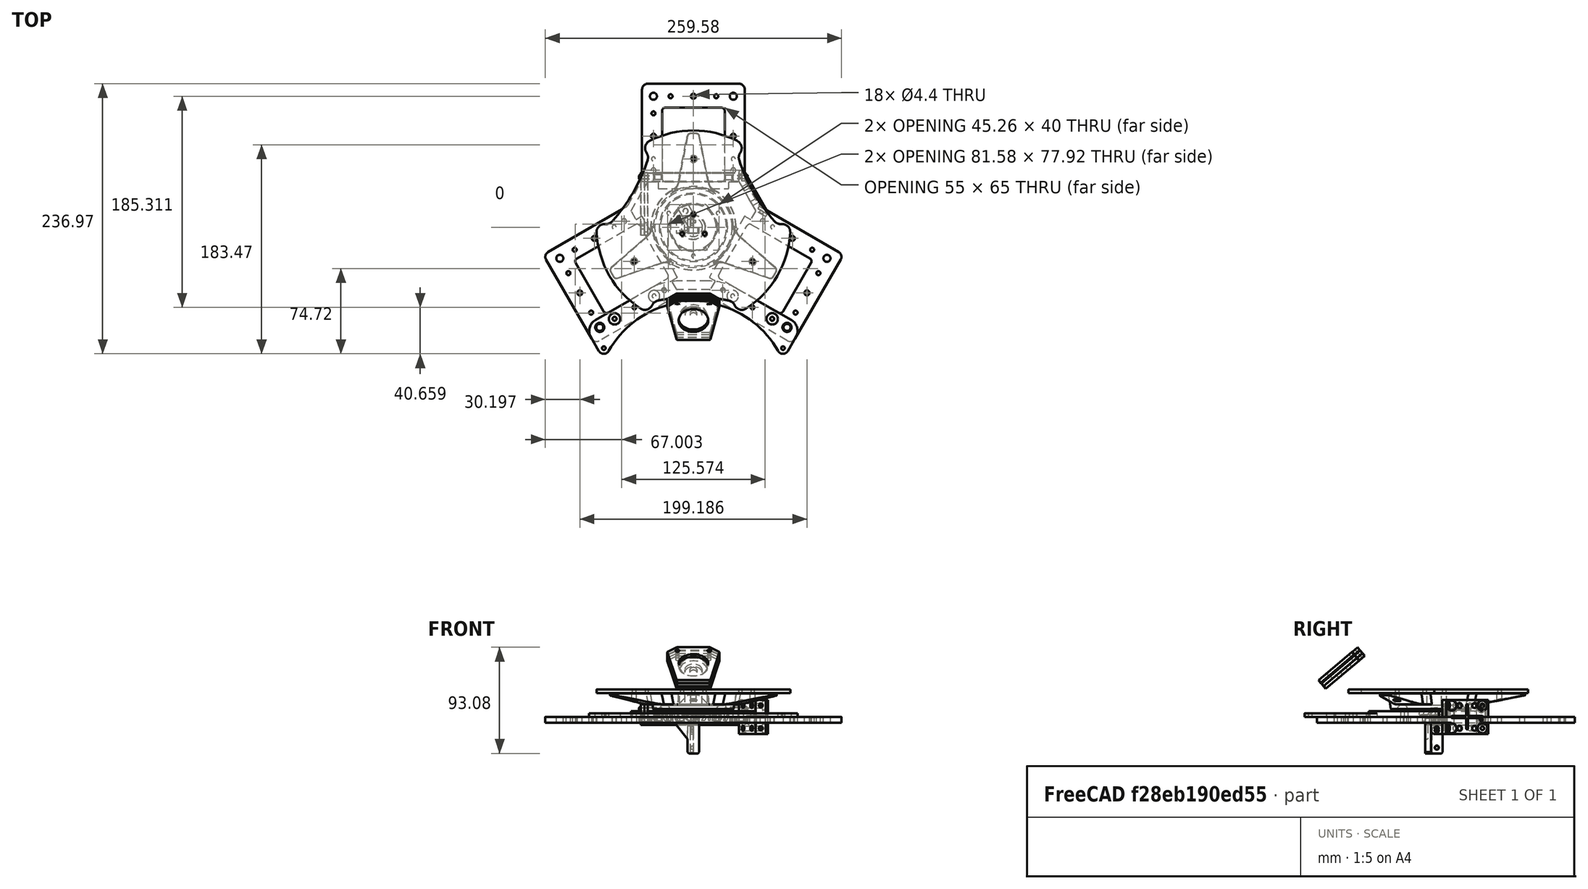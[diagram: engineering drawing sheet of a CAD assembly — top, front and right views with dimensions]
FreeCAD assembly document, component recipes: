
FREECAD ASSEMBLY — COMPONENT RECIPES ("structures")

This assembly document has 14 components, labeled P0..P13 below (a component is one placed body or linked part). 12 of them carry a construction recipe — the FreeCAD feature program that regenerates the part from scratch, quoted from this document or its linked companion documents; the rest are supplied as boundary geometry only. No exploded tour is included for this assembly.
NOTE — document 2 of 2 of this assembly tour. The two overview renders and the header above are repeated from document 1; the component sections below continue where the previous document stopped.
COMPONENT P11 — recipe-attached ("CoinTirette", modeled in this document).
Construction recipe (the document's own serialized feature program — sketch geometry with constraints, then the solid features built on it; lengths are millimeters unless a unit is written):

FEATURE [PartDesign::FeatureBase] Clone
  BaseFeature = -> Body030
  InvalidShape = false
  NewSolid = false
  Suppress = false
  TreeRank = 0
  ValidateShape = true
FEATURE [Sketcher::SketchObject] Sketch068
  ArcFitTolerance = 0
  AttachmentSupport = -> [Clone]
  ExternalBSplineMaxDegree = 0
  ExternalBSplineTolerance = 0
  ExternalGeometry = -> [Clone]
  FullyConstrained = true
  InternalTolerance = 1e-06
  InvalidShape = false
  MakeInternals = false
  MapMode = 5
  Placement = pos=(-3.09e-14,-52.3388,62.375) rot=(1,0,0;0.698132rad)
  Support = -> [Clone]
  TreeRank = 0
  ValidateShape = true
  sketch-geometry (2):
    g0: Circle CenterX=0 CenterY=-32.5627 CenterZ=0 NormalX=0 NormalY=0 NormalZ=1 AngleXU=0 Radius=3
    g1: Circle CenterX=0 CenterY=-32.5627 CenterZ=0 NormalX=0 NormalY=0 NormalZ=1 AngleXU=0 Radius=15
  constraints (4):
    c: Coincident(g0,g-3)
    c: Coincident(g1,g0)
    c: Diameter(g1) = 30
    c: Diameter(g0) = 6
FEATURE [PartDesign::Pad] Pad037
  AddSubType = 0
  AutoTaperInnerAngle = false
  BaseFeature = -> Clone
  CheckUpToFaceLimits = true
  ClaimChildren = false
  Direction = (-4e-16,-0.642788,0.766044)
  Fit = 0
  FitJoin = 0
  InnerFit = 0
  InnerFitJoin = 0
  InvalidShape = false
  Length = 10
  Length2 = 100
  Linearize = true
  NewSolid = false
  Profile = -> Sketch068
  Refine = true
  Suppress = false
  TaperInnerAngle = 0
  TaperInnerAngleRev = 0
  TreeRank = 0
  Type = 3
  UpToFace = -> Clone [Face2]
  ValidateShape = true
  _ProfileBasedVersion = 1
FEATURE [PartDesign::Body] Body032  label="PlateTirette_1"
  AutoGroupSolids = false
  BaseFeature = -> Body030
  ClaimAllChildren = false
  ExportMode = 0
  Group = -> [Clone,Sketch068,Pad037]
  InvalidShape = false
  Origin = -> Origin051
  SingleSolid = true
  Tip = -> Pad037
  TreeRank = 0
  ValidateShape = true
  _ExportChildren = -> [Clone,Pad037]
  _GroupVersion = 1
FEATURE [PartDesign::SubShapeBinder] Binder001  label="Binder001(Pad037)"
  BindCopyOnChange = 0
  BindMode = 2
  ClaimChildren = false
  Context = -> Part011 [Body033.Binder001.]
  EdgeTolerance = 1e-06
  FillStyle = 0
  Fuse = false
  InvalidShape = false
  MakeFace = true
  MergeEdges = true
  OffsetFill = false
  OffsetIntersection = false
  OffsetJoinType = 0
  OffsetOpenResult = false
  Outline = false
  PartialLoad = false
  Refine = true
  Relative = true
  SplitEdges = false
  TightBound = false
  TreeRank = 0
  ValidateShape = true
  _Version = 8
FEATURE [PartDesign::Pad] Pad038
  AddSubType = 0
  AutoTaperInnerAngle = false
  CheckUpToFaceLimits = true
  ClaimChildren = false
  Direction = (-4e-16,-0.642788,0.766044)
  Fit = 0
  FitJoin = 0
  InnerFit = 0
  InnerFitJoin = 0
  InvalidShape = false
  Length = 3
  Length2 = 100
  Linearize = true
  NewSolid = false
  Profile = -> Binder001
  Refine = true
  Suppress = false
  TaperInnerAngle = 0
  TaperInnerAngleRev = 0
  TreeRank = 0
  Type = 0
  ValidateShape = true
  _ProfileBasedVersion = 1
FEATURE [Sketcher::SketchObject] Sketch069
  ArcFitTolerance = 0
  AttachmentSupport = -> [Pad038]
  ExternalBSplineMaxDegree = 0
  ExternalBSplineTolerance = 0
  ExternalGeometry = -> [Pad038]
  FullyConstrained = true
  InternalTolerance = 1e-06
  InvalidShape = false
  MakeInternals = false
  MapMode = 5
  Placement = pos=(-3.46e-14,-54.2672,64.6731) rot=(1,0,0;0.698132rad)
  Support = -> [Pad038]
  TreeRank = 0
  ValidateShape = true
  sketch-geometry (1):
    g0: Circle CenterX=0 CenterY=-32.5627 CenterZ=0 NormalX=0 NormalY=0 NormalZ=1 AngleXU=0 Radius=12
  constraints (2):
    c: Coincident(g0,g-3)
    c: Diameter(g0) = 24
FEATURE [PartDesign::Pocket] Pocket030
  AddSubType = 1
  AutoTaperInnerAngle = false
  BaseFeature = -> Pad038
  CheckUpToFaceLimits = true
  ClaimChildren = false
  Direction = (1,1,1)
  Fit = 0
  FitJoin = 0
  InnerFit = 0
  InnerFitJoin = 0
  InvalidShape = false
  Length = 5
  Length2 = 100
  Linearize = true
  NewSolid = false
  Profile = -> Sketch069
  Refine = true
  Suppress = false
  TaperInnerAngle = 0
  TaperInnerAngleRev = 0
  TreeRank = 0
  Type = 1
  ValidateShape = true
  _ProfileBasedVersion = 1
  _Version = 1
FEATURE [PartDesign::Body] Body033  label="PlateTirette_2"
  AutoGroupSolids = false
  ClaimAllChildren = false
  ExportMode = 0
  Group = -> [Binder001,Pad038,Sketch069,Pocket030]
  InvalidShape = false
  Origin = -> Origin052
  SingleSolid = true
  Tip = -> Pocket030
  TreeRank = 0
  ValidateShape = true
  _ExportChildren = -> [Pad038,Pocket030]
  _GroupVersion = 1
FEATURE [PartDesign::SubShapeBinder] Binder002  label="Binder002(Pocket030)"
  BindCopyOnChange = 0
  BindMode = 0
  ClaimChildren = false
  Context = -> Part011 [Body034.Binder002.]
  EdgeTolerance = 1e-06
  FillStyle = 0
  Fuse = false
  InvalidShape = false
  MakeFace = true
  MergeEdges = true
  OffsetFill = false
  OffsetIntersection = false
  OffsetJoinType = 0
  OffsetOpenResult = false
  Outline = false
  PartialLoad = false
  Refine = true
  Relative = true
  SplitEdges = false
  Support = -> [Body033[Pocket030.Face5]]
  TightBound = false
  TreeRank = 0
  ValidateShape = true
  _Version = 8
FEATURE [PartDesign::Pad] Pad039
  AddSubType = 0
  AutoTaperInnerAngle = false
  CheckUpToFaceLimits = true
  ClaimChildren = false
  Direction = (-4e-16,-0.642788,0.766044)
  Fit = 0
  FitJoin = 0
  InnerFit = 0
  InnerFitJoin = 0
  InvalidShape = false
  Length = 0.8
  Length2 = 100
  Linearize = true
  NewSolid = false
  Profile = -> Binder002
  Refine = true
  Suppress = false
  TaperInnerAngle = 0
  TaperInnerAngleRev = 0
  TreeRank = 0
  Type = 0
  ValidateShape = true
  _ProfileBasedVersion = 1
FEATURE [Sketcher::SketchObject] Sketch070
  ArcFitTolerance = 0
  AttachmentSupport = -> [Pad039]
  ExternalBSplineMaxDegree = 0
  ExternalBSplineTolerance = 0
  ExternalGeometry = -> [Pad039]
  FullyConstrained = true
  InternalTolerance = 1e-06
  InvalidShape = false
  MakeInternals = false
  MapMode = 5
  Placement = pos=(-3.49e-14,-54.7814,65.286) rot=(1,0,0;0.698132rad)
  Support = -> [Pad039]
  TreeRank = 0
  ValidateShape = true
  sketch-geometry (1):
    g0: Circle CenterX=0 CenterY=-32.5627 CenterZ=0 NormalX=0 NormalY=0 NormalZ=1 AngleXU=0 Radius=15
  constraints (2):
    c: Coincident(g0,g-3)
    c: Diameter(g0) = 30
FEATURE [PartDesign::Pad] Pad040
  AddSubType = 0
  AutoTaperInnerAngle = false
  BaseFeature = -> Pad039
  CheckUpToFaceLimits = true
  ClaimChildren = false
  Direction = (-4e-16,-0.642788,0.766044)
  Fit = 0
  FitJoin = 0
  InnerFit = 0
  InnerFitJoin = 0
  InvalidShape = false
  Length = 10
  Length2 = 100
  Linearize = true
  NewSolid = false
  Profile = -> Sketch070
  Refine = true
  Reversed = true
  Suppress = false
  TaperInnerAngle = 0
  TaperInnerAngleRev = 0
  TreeRank = 0
  Type = 3
  UpToFace = -> Pad039 [Face16]
  ValidateShape = true
  _ProfileBasedVersion = 1
FEATURE [PartDesign::Body] Body034  label="InterPlateTirette"
  AutoGroupSolids = false
  ClaimAllChildren = false
  ExportMode = 0
  Group = -> [Binder002,Pad039,Sketch070,Pad040]
  InvalidShape = false
  Origin = -> Origin053
  SingleSolid = true
  Tip = -> Pad040
  TreeRank = 0
  ValidateShape = true
  _ExportChildren = -> [Pad039,Pad040]
  _GroupVersion = 1
FEATURE [PartDesign::SubShapeBinder] Binder003  label="Binder003(Pad040)"
  BindCopyOnChange = 0
  BindMode = 2
  ClaimChildren = false
  Context = -> Part011 [Body035.Binder003.]
  EdgeTolerance = 1e-06
  FillStyle = 0
  Fuse = false
  InvalidShape = false
  MakeFace = true
  MergeEdges = true
  OffsetFill = false
  OffsetIntersection = false
  OffsetJoinType = 0
  OffsetOpenResult = false
  Outline = false
  PartialLoad = false
  Refine = true
  Relative = true
  SplitEdges = false
  TightBound = false
  TreeRank = 0
  ValidateShape = true
  _Version = 8
FEATURE [PartDesign::Pad] Pad041
  AddSubType = 0
  AutoTaperInnerAngle = false
  CheckUpToFaceLimits = true
  ClaimChildren = false
  Direction = (-4e-16,-0.642788,0.766044)
  Fit = 0
  FitJoin = 0
  InnerFit = 0
  InnerFitJoin = 0
  InvalidShape = false
  Length = 3
  Length2 = 100
  Linearize = true
  NewSolid = false
  Profile = -> Binder003
  Refine = true
  Suppress = false
  TaperInnerAngle = 0
  TaperInnerAngleRev = 0
  TreeRank = 0
  Type = 0
  ValidateShape = true
  _ProfileBasedVersion = 1
FEATURE [Part::SubShapeBinder] Import  label="Import(Pocket030)"
  BindCopyOnChange = 0
  BindMode = 0
  ClaimChildren = false
  Context = -> Part011 [Body035.Import.]
  EdgeTolerance = 1e-06
  FillStyle = 0
  Fuse = false
  InvalidShape = false
  MakeFace = false
  MergeEdges = true
  OffsetFill = false
  OffsetIntersection = false
  OffsetJoinType = 0
  OffsetOpenResult = false
  Outline = false
  PartialLoad = false
  Refine = true
  Relative = true
  SplitEdges = false
  Support = -> [Body033[Pocket030.]]
  TightBound = false
  TreeRank = 0
  ValidateShape = true
  _Version = 8
FEATURE [Sketcher::SketchObject] Sketch071
  ArcFitTolerance = 0
  AttachmentSupport = -> [Pad041]
  ExternalBSplineMaxDegree = 0
  ExternalBSplineTolerance = 0
  ExternalGeometry = -> [Import]
  FullyConstrained = true
  InternalTolerance = 1e-06
  InvalidShape = false
  MakeInternals = false
  MapMode = 5
  Placement = pos=(-3.62e-14,-56.7098,67.5841) rot=(1,0,0;0.698132rad)
  Support = -> [Pad041]
  TreeRank = 0
  ValidateShape = true
  sketch-geometry (2):
    g0: Circle CenterX=0 CenterY=-32.5627 CenterZ=0 NormalX=0 NormalY=0 NormalZ=1 AngleXU=0 Radius=13
    g1: LineSegment [constr] StartX=-1.96e-14 StartY=-55.0073 StartZ=0 EndX=1.98e-14 EndY=-10.1181 EndZ=0
  constraints (5):
    c: PointOnObject(g0,g-2)
    c: Diameter(g0) = 26
    c: PointOnObject(g1,g-4)
    c: Symmetric(g-3,g-3,g1)
    c: Symmetric(g1,g1,g0)
FEATURE [PartDesign::Pocket] Pocket031
  AddSubType = 1
  AutoTaperInnerAngle = false
  BaseFeature = -> Pad041
  CheckUpToFaceLimits = true
  ClaimChildren = false
  Direction = (1,1,1)
  Fit = 0
  FitJoin = 0
  InnerFit = 0
  InnerFitJoin = 0
  InvalidShape = false
  Length = 5
  Length2 = 100
  Linearize = true
  NewSolid = false
  Profile = -> Sketch071
  Refine = true
  Suppress = false
  TaperInnerAngle = 0
  TaperInnerAngleRev = 0
  TreeRank = 0
  Type = 1
  ValidateShape = true
  _ProfileBasedVersion = 1
  _Version = 1
FEATURE [PartDesign::Body] Body035  label="PlateTirette_3"
  AutoGroupSolids = false
  ClaimAllChildren = false
  ExportMode = 0
  Group = -> [Binder003,Pad041,Sketch071,Import,Pocket031]
  InvalidShape = false
  Origin = -> Origin054
  SingleSolid = true
  Tip = -> Pocket031
  TreeRank = 0
  ValidateShape = true
  _ExportChildren = -> [Pad041,Import,Pocket031]
  _GroupVersion = 1
COMPONENT P12 — recipe-attached ("CoinLogo", modeled in this document).
Construction recipe (the document's own serialized feature program — sketch geometry with constraints, then the solid features built on it; lengths are millimeters unless a unit is written):

FEATURE [PartDesign::SubShapeBinder] Binder004  label="Binder004(Chamfer023)"
  BindCopyOnChange = 0
  BindMode = 0
  ClaimChildren = false
  Context = -> Part012 [Body036.Binder004.]
  EdgeTolerance = 1e-06
  FillStyle = 0
  Fuse = false
  InvalidShape = false
  MakeFace = true
  MergeEdges = true
  OffsetFill = false
  OffsetIntersection = false
  OffsetJoinType = 0
  OffsetOpenResult = false
  Outline = false
  PartialLoad = false
  Refine = true
  Relative = true
  SplitEdges = false
  Support = -> [Chamfer023[Face30]]
  TightBound = false
  TreeRank = 0
  ValidateShape = true
  _Version = 8
FEATURE [Sketcher::SketchObject] Sketch072
  ArcFitTolerance = 0
  AttachmentSupport = -> [Binder004]
  ExternalBSplineMaxDegree = 0
  ExternalBSplineTolerance = 0
  ExternalGeometry = -> [Binder004]
  FullyConstrained = true
  InternalTolerance = 1e-06
  InvalidShape = false
  MakeInternals = false
  MapMode = 5
  Placement = pos=(-2.82e-14,-50.4105,60.0769) rot=(1,0,0;0.698132rad)
  Support = -> [Binder004]
  TreeRank = 0
  ValidateShape = true
  sketch-geometry (2):
    g0: Circle CenterX=-14 CenterY=-14.7181 CenterZ=0 NormalX=0 NormalY=0 NormalZ=1 AngleXU=0 Radius=1.6
    g1: Circle CenterX=14 CenterY=-14.7181 CenterZ=0 NormalX=0 NormalY=0 NormalZ=1 AngleXU=0 Radius=1.6
  constraints (4):
    c: Coincident(g0,g-10)
    c: Coincident(g1,g-9)
    c: Diameter(g1) = 3.2
    c: Equal(g1,g0)
FEATURE [PartDesign::Pad] Pad042
  AddSubType = 0
  AutoTaperInnerAngle = false
  CheckUpToFaceLimits = true
  ClaimChildren = false
  Direction = (1,1,1)
  Fit = 0
  FitJoin = 0
  InnerFit = 0
  InnerFitJoin = 0
  InvalidShape = false
  Length = 3
  Length2 = 100
  Linearize = true
  NewSolid = false
  Profile = -> Sketch072
  Refine = true
  Suppress = false
  TaperInnerAngle = 0
  TaperInnerAngleRev = 0
  TreeRank = 0
  Type = 0
  ValidateShape = true
  _ProfileBasedVersion = 1
FEATURE [Part::Part2DObjectPython] ShapeString001  # Draft 2D object (typed FeaturePython)
  FontFile = <userpath>/Downloads/baveuse/baveuse.ttf
  InvalidShape = false
  Placement = pos=(-9,-91.52,42.09) rot=(1,0,0;0.698132rad)
  Size = 10
  String = K
  Tracking = 0
  TreeRank = 0
  ValidateShape = true
FEATURE [PartDesign::SubShapeBinder] Import001  label="Import001(ShapeString001)"
  BindCopyOnChange = 0
  BindMode = 0
  ClaimChildren = false
  Context = -> Part012 [Body036.Import001.]
  EdgeTolerance = 1e-06
  FillStyle = 0
  Fuse = false
  InvalidShape = false
  MakeFace = false
  MergeEdges = true
  OffsetFill = false
  OffsetIntersection = false
  OffsetJoinType = 0
  OffsetOpenResult = false
  Outline = false
  PartialLoad = false
  Refine = true
  Relative = true
  SplitEdges = false
  Support = -> [ShapeString001]
  TightBound = false
  TreeRank = 0
  ValidateShape = true
  _Version = 8
FEATURE [PartDesign::Pocket] Pocket032
  AddSubType = 1
  AutoTaperInnerAngle = false
  BaseFeature = -> Pad042
  CheckUpToFaceLimits = true
  ClaimChildren = false
  Direction = (1,1,1)
  Fit = 0
  FitJoin = 0
  InnerFit = 0
  InnerFitJoin = 0
  InvalidShape = false
  Length = 10
  Length2 = 100
  Linearize = true
  NewSolid = false
  Profile = -> Import001
  Refine = true
  Suppress = false
  TaperInnerAngle = 0
  TaperInnerAngleRev = 0
  TreeRank = 0
  Type = 0
  ValidateShape = true
  _ProfileBasedVersion = 1
  _Version = 1
FEATURE [PartDesign::Chamfer] Chamfer024
  AddSubType = 0
  Angle = 45
  Base = -> Pocket032 [Edge48,Edge49,Edge8,Edge5,Edge1,Edge2]
  BaseFeature = -> Pocket032
  ChamferType = 0
  FlipDirection = false
  InvalidShape = false
  NewSolid = false
  Refine = true
  Size = 0.4
  Size2 = 1
  SupportTransform = false
  Suppress = false
  TreeRank = 0
  UseAllEdges = false
  ValidateShape = true
FEATURE [PartDesign::Body] Body036  label="PlateLogo"
  AutoGroupSolids = false
  ClaimAllChildren = false
  ExportMode = 0
  Group = -> [Binder004,Sketch072,Pad042,ShapeString001,Import001,Pocket032,Chamfer024]
  InvalidShape = false
  Origin = -> Origin056
  SingleSolid = true
  Tip = -> Chamfer024
  TreeRank = 0
  ValidateShape = true
  _ExportChildren = -> [Binder004,Pad042,ShapeString001,Pocket032,Chamfer024]
  _GroupVersion = 1
FEATURE [PartDesign::FeatureBase] Clone001
  BaseFeature = -> Pad042
  InvalidShape = false
  NewSolid = false
  Suppress = false
  TreeRank = 10
  ValidateShape = true
FEATURE [Sketcher::SketchObject] Sketch073
  ArcFitTolerance = 0
  AttachmentSupport = -> [Clone001]
  ExternalBSplineMaxDegree = 0
  ExternalBSplineTolerance = 0
  ExternalGeometry = -> [Clone001]
  FullyConstrained = true
  InternalTolerance = 1e-06
  InvalidShape = false
  MakeInternals = false
  MapMode = 5
  Placement = pos=(-3.18e-14,-52.3388,62.375) rot=(1,0,0;0.698132rad)
  Support = -> [Clone001]
  TreeRank = 12
  ValidateShape = true
  sketch-geometry (1):
    g0: Circle CenterX=0 CenterY=-32.5673 CenterZ=0 NormalX=0 NormalY=0 NormalZ=1 AngleXU=0 Radius=7.5
  constraints (3):
    c: PointOnObject(g0,g-2)
    c: DistanceY(g-3,g0) = 22.44
    c: Diameter(g0) = 15
FEATURE [PartDesign::Pocket] Pocket033
  AddSubType = 1
  AutoTaperInnerAngle = false
  BaseFeature = -> Clone001
  CheckUpToFaceLimits = true
  ClaimChildren = false
  Direction = (1,1,1)
  Fit = 0
  FitJoin = 0
  InnerFit = 0
  InnerFitJoin = 0
  InvalidShape = false
  Length = 5
  Length2 = 100
  Linearize = true
  NewSolid = false
  Profile = -> Sketch073
  Refine = true
  Suppress = false
  TaperInnerAngle = 0
  TaperInnerAngleRev = 0
  TreeRank = 13
  Type = 1
  ValidateShape = true
  _ProfileBasedVersion = 1
  _Version = 1
FEATURE [PartDesign::Body] Body037  label="PlateInit"
  AutoGroupSolids = false
  BaseFeature = -> Pad042
  ClaimAllChildren = false
  ExportMode = 0
  Group = -> [Clone001,Sketch073,Pocket033]
  InvalidShape = false
  Origin = -> Origin057
  SingleSolid = true
  Tip = -> Pocket033
  TreeRank = 11
  ValidateShape = true
  _ExportChildren = -> [Clone001,Pocket033]
  _GroupVersion = 1
COMPONENT P13 — recipe-attached ("RobotStand", modeled in this document).
Construction recipe (the document's own serialized feature program — sketch geometry with constraints, then the solid features built on it; lengths are millimeters unless a unit is written):

FEATURE [Sketcher::SketchObject] Sketch074
  ArcFitTolerance = 1e-06
  AttachmentSupport = -> [XY_Plane047]
  ExternalBSplineMaxDegree = 5
  ExternalBSplineTolerance = 0.0001
  FullyConstrained = true
  InternalTolerance = 1e-06
  InvalidShape = false
  MakeInternals = true
  MapMode = 5
  Support = -> [XY_Plane047]
  TreeRank = 105
  ValidateShape = true
  sketch-geometry (1):
    g0: Circle CenterX=0 CenterY=0 CenterZ=0 NormalX=0 NormalY=0 NormalZ=1 AngleXU=0 Radius=10
  constraints (2):
    c: Coincident(g0,g-1)
    c: Diameter(g0) = 20
FEATURE [PartDesign::Pad] Pad043
  AddSubType = 0
  AlongSketchNormal = false
  AutoTaperInnerAngle = true
  CheckUpToFaceLimits = true
  ClaimChildren = false
  Direction = (0,0,1)
  Fit = 0
  FitJoin = 0
  InnerFit = 0
  InnerFitJoin = 0
  InvalidShape = false
  Length = 4
  Length2 = 100
  Linearize = true
  NewSolid = false
  Profile = -> Sketch074
  Refine = true
  Suppress = false
  TaperAngle = 10
  TaperInnerAngle = -10
  TaperInnerAngleRev = 0
  TreeRank = 106
  Type = 0
  ValidateShape = true
  _ProfileBasedVersion = 1
FEATURE [PartDesign::Pad] Pad044
  AddSubType = 0
  AlongSketchNormal = false
  AutoTaperInnerAngle = true
  BaseFeature = -> Pad043
  CheckUpToFaceLimits = true
  ClaimChildren = false
  Direction = (0,0,1)
  Fit = 0
  FitJoin = 0
  InnerFit = 0
  InnerFitJoin = 0
  InvalidShape = false
  Length = 2
  Length2 = 100
  Linearize = true
  NewSolid = false
  Profile = -> Pad043 [Face3]
  Refine = true
  Suppress = false
  TaperInnerAngle = 0
  TaperInnerAngleRev = 0
  TreeRank = 107
  Type = 0
  ValidateShape = true
  _ProfileBasedVersion = 1
FEATURE [Sketcher::SketchObject] Sketch075
  ArcFitTolerance = 1e-06
  AttachmentSupport = -> [Pad044]
  ExternalBSplineMaxDegree = 5
  ExternalBSplineTolerance = 0.0001
  FullyConstrained = true
  InternalTolerance = 1e-06
  InvalidShape = false
  MakeInternals = true
  MapMode = 5
  Placement = pos=(0,0,6) rot=(0,0,1;0rad)
  Support = -> [Pad044]
  TreeRank = 108
  ValidateShape = true
  sketch-geometry (1):
    g0: Circle CenterX=0 CenterY=0 CenterZ=0 NormalX=0 NormalY=0 NormalZ=1 AngleXU=0 Radius=35
  constraints (2):
    c: Coincident(g0,g-1)
    c: Diameter(g0) = 70
FEATURE [PartDesign::Pad] Pad045
  AddSubType = 0
  AlongSketchNormal = false
  AutoTaperInnerAngle = true
  BaseFeature = -> Pad044
  CheckUpToFaceLimits = true
  ClaimChildren = false
  Direction = (0,0,1)
  Fit = 0
  FitJoin = 0
  InnerFit = 0
  InnerFitJoin = 0
  InvalidShape = false
  Length = 15
  Length2 = 100
  Linearize = true
  NewSolid = false
  Profile = -> Sketch075
  Refine = true
  Suppress = false
  TaperAngle = 10
  TaperInnerAngle = -10
  TaperInnerAngleRev = 0
  TreeRank = 109
  Type = 0
  ValidateShape = true
  _ProfileBasedVersion = 1
FEATURE [Part::SubShapeBinder] Import002  label="Import002(Fillet011)"
  BindCopyOnChange = 0
  BindMode = 0
  ClaimChildren = false
  Context = -> Group002 [Body038.Import002.]
  EdgeTolerance = 1e-06
  FillStyle = 0
  Fuse = false
  InvalidShape = false
  MakeFace = false
  MergeEdges = true
  OffsetFill = false
  OffsetIntersection = false
  OffsetJoinType = 0
  OffsetOpenResult = false
  Outline = false
  PartialLoad = false
  Relative = true
  SplitEdges = false
  Support = -> [Link075[Fillet011.]]
  TightBound = false
  TreeRank = 110
  ValidateShape = true
  _Version = 8
FEATURE [Sketcher::SketchObject] Sketch076
  ArcFitTolerance = 1e-06
  AttachmentSupport = -> [YZ_Plane047]
  ExternalBSplineMaxDegree = 5
  ExternalBSplineTolerance = 0.0001
  ExternalGeometry = -> [Pad045]
  FullyConstrained = true
  InternalTolerance = 1e-06
  InvalidShape = false
  MakeInternals = true
  MapMode = 5
  Placement = pos=(0,0,0) rot=(0.57735,0.57735,0.57735;2.0944rad)
  Support = -> [YZ_Plane047]
  TreeRank = 111
  ValidateShape = true
  sketch-geometry (5):
    g0: LineSegment StartX=21 StartY=6 StartZ=0 EndX=29 EndY=6 EndZ=0
    g1: LineSegment StartX=29 StartY=6 StartZ=0 EndX=29 EndY=10 EndZ=0
    g2: LineSegment StartX=29 StartY=10 StartZ=0 EndX=21 EndY=10 EndZ=0
    g3: LineSegment StartX=21 StartY=10 StartZ=0 EndX=21 EndY=6 EndZ=0
    g4: LineSegment [constr] StartX=25 StartY=6 StartZ=0 EndX=25 EndY=10 EndZ=0
  constraints (15):
    c: Coincident(g0,g1)
    c: Coincident(g1,g2)
    c: Coincident(g2,g3)
    c: Coincident(g3,g0)
    c: Horizontal(g0)
    c: Horizontal(g2)
    c: Vertical(g1)
    c: Vertical(g3)
    c: PointOnObject(g4,g2)
    c: Vertical(g4)
    c: Symmetric(g0,g0,g4)
    c: DistanceX(g4) = 25
    c: DistanceX(g0,g0) = 8
    c: PointOnObject(g0,g-3)
    c: DistanceY(g1,g1) = 4
FEATURE [PartDesign::Groove] Groove
  AddSubType = 1
  Angle = 360
  Axis = (-2e-16,3e-16,1)
  Base = (0,0,0)
  BaseFeature = -> Pad045
  ClaimChildren = false
  Fit = 0
  FitJoin = 0
  InnerFit = 0
  InnerFitJoin = 0
  InvalidShape = false
  Linearize = true
  NewSolid = false
  Profile = -> Sketch076
  ReferenceAxis = -> Sketch076 [V_Axis]
  Refine = true
  Suppress = false
  TreeRank = 112
  ValidateShape = true
  _ProfileBasedVersion = 1
FEATURE [Sketcher::SketchObject] Sketch077
  ArcFitTolerance = 1e-06
  AttachmentSupport = -> [Groove]
  ExternalBSplineMaxDegree = 5
  ExternalBSplineTolerance = 0.0001
  FullyConstrained = true
  InternalTolerance = 1e-06
  InvalidShape = false
  MakeInternals = true
  MapMode = 5
  Placement = pos=(0,0,21) rot=(0,0,1;0rad)
  Support = -> [Groove]
  TreeRank = 113
  ValidateShape = true
  sketch-geometry (7):
    g0: Circle CenterX=-4.7166e-12 CenterY=11.3561 CenterZ=0 NormalX=0 NormalY=0 NormalZ=1 AngleXU=0 Radius=2.2
    g1: Circle CenterX=9.83464 CenterY=-5.67803 CenterZ=0 NormalX=0 NormalY=0 NormalZ=1 AngleXU=0 Radius=2.2
    g2: Circle CenterX=-9.83464 CenterY=-5.67803 CenterZ=0 NormalX=0 NormalY=0 NormalZ=1 AngleXU=0 Radius=2.2
    g3: Circle [constr] CenterX=7.482e-13 CenterY=1.30938e-11 CenterZ=0 NormalX=0 NormalY=0 NormalZ=1 AngleXU=0 Radius=11.3561
    g4: LineSegment [constr] StartX=-9.83464 StartY=-5.67803 StartZ=0 EndX=7.478e-13 EndY=1.30935e-11 EndZ=0
    g5: LineSegment [constr] StartX=7.482e-13 StartY=1.30938e-11 StartZ=0 EndX=9.83464 EndY=-5.67803 EndZ=0
    g6: LineSegment [constr] StartX=7.482e-13 StartY=1.30938e-11 StartZ=0 EndX=-4.7166e-12 EndY=11.3561 EndZ=0
  constraints (16):
    c: PointOnObject(g0,g-2)
    c: Coincident(g3,g-1)
    c: PointOnObject(g0,g3)
    c: PointOnObject(g1,g3)
    c: PointOnObject(g2,g3)
    c: Equal(g2,g1)
    c: Equal(g1,g0)
    c: Coincident(g4,g2)
    c: Coincident(g4,g3)
    c: Coincident(g5,g3)
    c: Coincident(g5,g1)
    c: Coincident(g6,g3)
    c: Coincident(g6,g0)
    c: Angle(g5,g6) = 2.0944
    c: Symmetric(g2,g1,g-2)
    c: Diameter(g1) = 4.4
FEATURE [PartDesign::Pocket] Pocket034
  AddSubType = 1
  AutoTaperInnerAngle = true
  BaseFeature = -> Groove
  CheckUpToFaceLimits = true
  ClaimChildren = false
  Direction = (1,1,1)
  Fit = 0
  FitJoin = 0
  InnerFit = 0
  InnerFitJoin = 0
  InvalidShape = false
  Length = 10
  Length2 = 100
  Linearize = true
  NewSolid = false
  Profile = -> Sketch077
  Refine = true
  Suppress = false
  TaperInnerAngle = 0
  TaperInnerAngleRev = 0
  TreeRank = 114
  Type = 0
  ValidateShape = true
  _ProfileBasedVersion = 1
  _Version = 1
FEATURE [PartDesign::Fillet] Fillet023
  AddSubType = 0
  Base = -> Pocket034 [Edge3]
  BaseFeature = -> Pocket034
  InvalidShape = false
  NewSolid = false
  Radius = 14
  Refine = true
  SupportTransform = false
  Suppress = false
  TreeRank = 115
  UseAllEdges = false
  ValidateShape = true
FEATURE [PartDesign::Chamfer] Chamfer025
  AddSubType = 0
  Angle = 45
  Base = -> Fillet023 [Edge3]
  BaseFeature = -> Fillet023
  ChamferType = 0
  FlipDirection = false
  InvalidShape = false
  NewSolid = false
  Refine = true
  Size = 2
  Size2 = 1
  SupportTransform = false
  Suppress = false
  TreeRank = 116
  UseAllEdges = false
  ValidateShape = true
FEATURE [PartDesign::Fillet] Fillet024
  AddSubType = 0
  Base = -> Chamfer025 [Edge13,Edge11]
  BaseFeature = -> Chamfer025
  InvalidShape = false
  NewSolid = false
  Radius = 2
  Refine = true
  SupportTransform = false
  Suppress = false
  TreeRank = 117
  UseAllEdges = false
  ValidateShape = true
FEATURE [PartDesign::Chamfer] Chamfer026
  AddSubType = 0
  Angle = 45
  Base = -> Fillet024 [Edge18,Edge3,Edge15]
  BaseFeature = -> Fillet024
  ChamferType = 0
  FlipDirection = false
  InvalidShape = false
  NewSolid = false
  Refine = true
  Size = 1
  Size2 = 1
  SupportTransform = false
  Suppress = false
  TreeRank = 118
  UseAllEdges = false
  ValidateShape = true
FEATURE [PartDesign::SubShapeBinder] Binder005  label="Binder005(Chamfer026)"
  BindCopyOnChange = 0
  BindMode = 0
  ClaimChildren = false
  Context = -> Group002 [Part013.Body039.Binder005.]
  EdgeTolerance = 1e-06
  FillStyle = 0
  Fuse = false
  InvalidShape = false
  MakeFace = true
  MergeEdges = true
  OffsetFill = false
  OffsetIntersection = false
  OffsetJoinType = 0
  OffsetOpenResult = false
  Outline = false
  PartialLoad = false
  Relative = true
  SplitEdges = false
  Support = -> [Body038[Chamfer026.Face17]]
  TightBound = false
  TreeRank = 133
  ValidateShape = true
  _Version = 8
FEATURE [Sketcher::SketchObject] Sketch078
  ArcFitTolerance = 1e-06
  AttachmentSupport = -> [Binder005]
  ExternalBSplineMaxDegree = 5
  ExternalBSplineTolerance = 0.0001
  FullyConstrained = true
  InternalTolerance = 1e-06
  InvalidShape = false
  MakeInternals = true
  MapMode = 5
  Placement = pos=(0,0,21) rot=(0,0,1;0rad)
  Support = -> [Binder005]
  TreeRank = 134
  ValidateShape = true
  sketch-geometry (12):
    g0: Circle CenterX=2.0355e-12 CenterY=-3.998e-13 CenterZ=0 NormalX=0 NormalY=0 NormalZ=1 AngleXU=0 Radius=85
    g1: Circle CenterX=2.0355e-12 CenterY=11.355 CenterZ=0 NormalX=0 NormalY=0 NormalZ=1 AngleXU=0 Radius=1.6
    g2: Circle CenterX=9.83372 CenterY=-5.6775 CenterZ=0 NormalX=0 NormalY=0 NormalZ=1 AngleXU=0 Radius=1.6
    g3: Circle CenterX=-9.83372 CenterY=-5.6775 CenterZ=0 NormalX=0 NormalY=0 NormalZ=1 AngleXU=0 Radius=1.6
    g4: Circle [constr] CenterX=2.0355e-12 CenterY=-3.998e-13 CenterZ=0 NormalX=0 NormalY=0 NormalZ=1 AngleXU=0 Radius=11.355
    g5: LineSegment [constr] StartX=2.0355e-12 StartY=11.355 StartZ=0 EndX=2.0355e-12 EndY=-3.997e-13 EndZ=0
    g6: LineSegment [constr] StartX=2.0355e-12 StartY=-3.998e-13 StartZ=0 EndX=-9.83372 EndY=-5.6775 EndZ=0
    g7: LineSegment [constr] StartX=2.0355e-12 StartY=-3.998e-13 StartZ=0 EndX=9.83372 EndY=-5.6775 EndZ=0
    g8: Circle CenterX=-3.78e-14 CenterY=60 CenterZ=0 NormalX=0 NormalY=0 NormalZ=1 AngleXU=0 Radius=1.6
    g9: Circle [constr] CenterX=2.0355e-12 CenterY=-3.998e-13 CenterZ=0 NormalX=0 NormalY=0 NormalZ=1 AngleXU=0 Radius=60
    g10: Circle CenterX=51.9615 CenterY=-30 CenterZ=0 NormalX=0 NormalY=0 NormalZ=1 AngleXU=0 Radius=1.6
    g11: Circle CenterX=-51.9615 CenterY=-30 CenterZ=0 NormalX=0 NormalY=0 NormalZ=1 AngleXU=0 Radius=1.6
  constraints (29):
    c: Coincident(g0,g-1)
    c: Diameter(g0) = 170
    c: Equal(g3,g2)
    c: Equal(g3,g1)
    c: Diameter(g3) = 3.2
    c: Coincident(g4,g0)
    c: PointOnObject(g1,g4)
    c: Diameter(g4) = 22.71
    c: Coincident(g5,g1)
    c: Coincident(g5,g0)
    c: Vertical(g5)
    c: Coincident(g6,g0)
    c: Coincident(g6,g3)
    c: Coincident(g7,g0)
    c: Coincident(g7,g2)
    c: Angle(g7,g5) = 2.0944
    c: Symmetric(g3,g2,g-2)
    c: PointOnObject(g2,g4)
    c: PointOnObject(g8,g-2)
    c: DistanceY(g8) = 60
    c: Equal(g8,g1)
    c: Coincident(g9,g0)
    c: PointOnObject(g8,g9)
    c: PointOnObject(g10,g9)
    c: PointOnObject(g11,g9)
    c: Equal(g11,g10)
    c: Equal(g10,g8)
    c: PointOnObject(g10,g7)
    c: PointOnObject(g11,g6)
FEATURE [PartDesign::Pad] Pad046
  AddSubType = 0
  AlongSketchNormal = false
  AutoTaperInnerAngle = true
  CheckUpToFaceLimits = true
  ClaimChildren = false
  Direction = (0,0,1)
  Fit = 0
  FitJoin = 0
  InnerFit = 0
  InnerFitJoin = 0
  InvalidShape = false
  Length = 3
  Length2 = 100
  Linearize = true
  NewSolid = false
  Profile = -> Sketch078
  Refine = true
  Suppress = false
  TaperInnerAngle = 0
  TaperInnerAngleRev = 0
  TreeRank = 135
  Type = 0
  ValidateShape = true
  _ProfileBasedVersion = 1
FEATURE [Sketcher::SketchObject] Sketch079
  ArcFitTolerance = 1e-06
  AttachmentSupport = -> [Chamfer026]
  ExternalBSplineMaxDegree = 5
  ExternalBSplineTolerance = 0.0001
  FullyConstrained = false
  InternalTolerance = 1e-06
  InvalidShape = false
  MakeInternals = true
  MapMode = 5
  Placement = pos=(0,0,21) rot=(0,0,1;0rad)
  Support = -> [Chamfer026]
  TreeRank = 136
  ValidateShape = true
  sketch-geometry (4):
    g0: ArcOfCircle CenterX=1.25182e-10 CenterY=4.9383e-12 CenterZ=0 NormalX=0 NormalY=0 NormalZ=1 AngleXU=0 Radius=34.3525 StartAngle=1.11893 EndAngle=2.02267
    g1: ArcOfCircle CenterX=1.25182e-10 CenterY=4.9383e-12 CenterZ=0 NormalX=0 NormalY=0 NormalZ=1 AngleXU=0 Radius=82.5 StartAngle=1.51015 EndAngle=1.63144
    g2: LineSegment StartX=-15 StartY=30.9046 StartZ=0 EndX=-5 EndY=82.3483 EndZ=0
    g3: LineSegment StartX=5 StartY=82.3483 StartZ=0 EndX=15 EndY=30.9046 EndZ=0
  constraints (11):
    c: Coincident(g0,g-1)
    c: Coincident(g1,g0)
    c: Symmetric(g1,g1,g-2)
    c: Symmetric(g0,g0,g-2)
    c: Coincident(g2,g0)
    c: Coincident(g2,g1)
    c: Coincident(g3,g1)
    c: Coincident(g3,g0)
    c: Diameter(g1) = 165
    c: DistanceX(g1,g1) = 10
    c: DistanceX(g0,g0) = 30
FEATURE [PartDesign::Pad] Pad047
  AddSubType = 0
  AlongSketchNormal = false
  AutoTaperInnerAngle = true
  BaseFeature = -> Chamfer026
  CheckUpToFaceLimits = true
  ClaimChildren = false
  Direction = (0,0,1)
  Fit = 0
  FitJoin = 0
  InnerFit = 0
  InnerFitJoin = 0
  InvalidShape = false
  Length = 10
  Length2 = 100
  Linearize = true
  NewSolid = false
  Profile = -> Sketch079
  Refine = true
  Reversed = true
  Suppress = false
  TaperInnerAngle = 0
  TaperInnerAngleRev = 0
  TreeRank = 137
  Type = 0
  ValidateShape = true
  _ProfileBasedVersion = 1
FEATURE [PartDesign::Chamfer] Chamfer027
  AddSubType = 0
  Angle = 45
  Base = -> Pad047 [Edge37]
  BaseFeature = -> Pad047
  ChamferType = 1
  FlipDirection = false
  InvalidShape = false
  NewSolid = false
  Refine = true
  Size = 40
  Size2 = 8
  SupportTransform = false
  Suppress = false
  TreeRank = 138
  UseAllEdges = false
  ValidateShape = true
FEATURE [PartDesign::Fillet] Fillet025
  AddSubType = 0
  Base = -> Chamfer027 [Edge3,Edge14]
  BaseFeature = -> Chamfer027
  InvalidShape = false
  NewSolid = false
  Radius = 10
  Refine = true
  SupportTransform = false
  Suppress = false
  TreeRank = 139
  UseAllEdges = false
  ValidateShape = true
FEATURE [PartDesign::Fillet] Fillet026
  AddSubType = 0
  Base = -> Fillet025 [Edge25,Edge5]
  BaseFeature = -> Fillet025
  InvalidShape = false
  NewSolid = false
  Radius = 3
  Refine = true
  SupportTransform = false
  Suppress = false
  TreeRank = 140
  UseAllEdges = false
  ValidateShape = true
FEATURE [PartDesign::Fillet] Fillet027
  AddSubType = 0
  Base = -> Fillet026 [Edge7]
  BaseFeature = -> Fillet026
  InvalidShape = false
  NewSolid = false
  Radius = 40
  Refine = true
  SupportTransform = false
  Suppress = false
  TreeRank = 141
  UseAllEdges = false
  ValidateShape = true
FEATURE [PartDesign::PolarPattern] PolarPattern
  AddSubType = 0
  Angle = 360
  Axis = -> Sketch079 [N_Axis]
  BaseFeature = -> Fillet027
  CopyShape = false
  InvalidShape = false
  NewSolid = false
  Occurrences = 3
  OriginalSubs = -> [Pad047,Chamfer027,Fillet025,Fillet026,Fillet027]
  Originals = -> [Pad047,Chamfer027,Fillet025,Fillet026,Fillet027]
  ParallelTransform = true
  Refine = true
  SubTransform = true
  Suppress = false
  TreeRank = 142
  ValidateShape = true
  _Version = 3
FEATURE [Sketcher::SketchObject] Sketch080
  ArcFitTolerance = 1e-06
  AttachmentSupport = -> [PolarPattern]
  ExternalBSplineMaxDegree = 5
  ExternalBSplineTolerance = 0.0001
  FullyConstrained = true
  InternalTolerance = 1e-06
  InvalidShape = false
  MakeInternals = true
  MapMode = 5
  Placement = pos=(0,0,21) rot=(0,0,1;0rad)
  Support = -> [PolarPattern]
  TreeRank = 143
  ValidateShape = true
  sketch-geometry (1):
    g0: Circle CenterX=0 CenterY=60 CenterZ=0 NormalX=0 NormalY=0 NormalZ=1 AngleXU=0 Radius=2.2
  constraints (3):
    c: PointOnObject(g0,g-2)
    c: Diameter(g0) = 4.4
    c: DistanceY(g-1,g0) = 60
FEATURE [PartDesign::Pocket] Pocket035
  AddSubType = 1
  AutoTaperInnerAngle = true
  BaseFeature = -> PolarPattern
  CheckUpToFaceLimits = true
  ClaimChildren = false
  Direction = (1,1,1)
  Fit = 0
  FitJoin = 0
  InnerFit = 0
  InnerFitJoin = 0
  InvalidShape = false
  Length = 5
  Length2 = 100
  Linearize = true
  NewSolid = false
  Profile = -> Sketch080
  Refine = true
  Suppress = false
  TaperInnerAngle = 0
  TaperInnerAngleRev = 0
  TreeRank = 144
  Type = 1
  ValidateShape = true
  _ProfileBasedVersion = 1
  _Version = 1
FEATURE [PartDesign::PolarPattern] PolarPattern016
  AddSubType = 0
  Angle = 360
  Axis = -> Sketch080 [N_Axis]
  BaseFeature = -> Pocket035
  CopyShape = false
  InvalidShape = false
  NewSolid = false
  Occurrences = 3
  OriginalSubs = -> [Pocket035]
  Originals = -> [Pocket035]
  ParallelTransform = true
  Refine = true
  SubTransform = true
  Suppress = false
  TreeRank = 145
  ValidateShape = true
  _Version = 3
FEATURE [PartDesign::Chamfer] Chamfer028
  AddSubType = 0
  Angle = 45
  Base = -> PolarPattern016 [Edge11,Edge114,Edge108]
  BaseFeature = -> PolarPattern016
  ChamferType = 0
  FlipDirection = false
  InvalidShape = false
  NewSolid = false
  Refine = true
  Size = 1
  Size2 = 1
  SupportTransform = false
  Suppress = false
  TreeRank = 146
  UseAllEdges = false
  ValidateShape = true
FEATURE [PartDesign::Chamfer] Chamfer029
  AddSubType = 0
  Angle = 45
  Base = -> Chamfer028 [Face11]
  BaseFeature = -> Chamfer028
  ChamferType = 0
  FlipDirection = false
  InvalidShape = false
  NewSolid = false
  Refine = true
  Size = 0.4
  Size2 = 1
  SupportTransform = false
  Suppress = false
  TreeRank = 147
  UseAllEdges = false
  ValidateShape = true
FEATURE [PartDesign::Body] Body038  label="PlugRobot"
  AutoGroupSolids = false
  ClaimAllChildren = false
  ExportMode = 0
  Group = -> [Sketch074,Pad043,Pad044,Sketch075,Pad045,Import002,Sketch076,Groove,Sketch077,Pocket034,Fillet023,Chamfer025,Fillet024,Chamfer026,Sketch079,Pad047,Chamfer027,Fillet025,Fillet026,Fillet027,PolarPattern,Sketch080,Pocket035,PolarPattern016,Chamfer028,Chamfer029]
  InvalidShape = false
  Origin = -> Origin059
  SingleSolid = true
  Tip = -> Chamfer029
  TreeRank = 104
  ValidateShape = true
  _ExportChildren = -> [Pad043,Pad044,Pad045,Import002,Groove,Pocket034,Fillet023,Chamfer025,Fillet024,Chamfer026,Pad047,Chamfer027,Fillet025,Fillet026,Fillet027,PolarPattern,Pocket035,PolarPattern016,Chamfer028,Chamfer029]
  _GroupVersion = 1
FEATURE [Sketcher::SketchObject] Sketch081
  ArcFitTolerance = 1e-06
  AttachmentSupport = -> [Pad046]
  ExternalBSplineMaxDegree = 5
  ExternalBSplineTolerance = 0.0001
  FullyConstrained = true
  InternalTolerance = 1e-06
  InvalidShape = false
  MakeInternals = true
  MapMode = 5
  Placement = pos=(0,0,24) rot=(0,0,1;0rad)
  Support = -> [Pad046]
  TreeRank = 148
  ValidateShape = true
  sketch-geometry (6):
    g0: LineSegment StartX=-40 StartY=-75 StartZ=0 EndX=-34.2265 EndY=-65 EndZ=0
    g1: ArcOfCircle CenterX=3.0925e-12 CenterY=-211.043 CenterZ=0 NormalX=0 NormalY=0 NormalZ=1 AngleXU=0 Radius=150 StartAngle=1.34059 EndAngle=1.801
    g2: ArcOfCircle CenterX=3.8288e-12 CenterY=2.3123e-12 CenterZ=0 NormalX=0 NormalY=0 NormalZ=1 AngleXU=0 Radius=85 StartAngle=4.22243 EndAngle=5.20235
    g3: LineSegment StartX=34.2265 StartY=-65 StartZ=0 EndX=40 EndY=-75 EndZ=0
    g4: LineSegment [constr] StartX=-40 StartY=-75 StartZ=0 EndX=-8.3276e-12 EndY=-5.71797 EndZ=0
    g5: LineSegment [constr] StartX=-8.3245e-12 StartY=-5.71797 StartZ=0 EndX=40 EndY=-75 EndZ=0
  constraints (18):
    c: PointOnObject(g1,g-2)
    c: Coincident(g1,g0)
    c: Coincident(g2,g-1)
    c: Coincident(g2,g0)
    c: Coincident(g3,g1)
    c: Coincident(g3,g2)
    c: Equal(g3,g0)
    c: Angle(g0,g3) = 1.0472
    c: Diameter(g1) = 300
    c: DistanceY(g0) = -65
    c: Diameter(g2) = 170
    c: Coincident(g4,g0)
    c: PointOnObject(g4,g-2)
    c: Coincident(g5,g4)
    c: Coincident(g5,g2)
    c: PointOnObject(g1,g5)
    c: PointOnObject(g0,g4)
    c: DistanceX(g0,g2) = 80
FEATURE [PartDesign::Pocket] Pocket036
  AddSubType = 1
  AutoTaperInnerAngle = true
  BaseFeature = -> Pad046
  CheckUpToFaceLimits = true
  ClaimChildren = false
  Direction = (1,1,1)
  Fit = 0
  FitJoin = 0
  InnerFit = 0
  InnerFitJoin = 0
  InvalidShape = false
  Length = 5
  Length2 = 100
  Linearize = true
  NewSolid = false
  Profile = -> Sketch081
  Refine = true
  Suppress = false
  TaperInnerAngle = 0
  TaperInnerAngleRev = 0
  TreeRank = 149
  Type = 1
  ValidateShape = true
  _ProfileBasedVersion = 1
  _Version = 1
FEATURE [PartDesign::Fillet] Fillet028
  AddSubType = 0
  Base = -> Pocket036 [Edge25,Edge14,Edge26,Edge13]
  BaseFeature = -> Pocket036
  InvalidShape = false
  NewSolid = false
  Radius = 7
  Refine = true
  SupportTransform = false
  Suppress = false
  TreeRank = 150
  UseAllEdges = false
  ValidateShape = true
FEATURE [PartDesign::PolarPattern] PolarPattern017
  AddSubType = 0
  Angle = 360
  Axis = -> Sketch081 [N_Axis]
  BaseFeature = -> Fillet028
  CopyShape = false
  InvalidShape = false
  NewSolid = false
  Occurrences = 3
  OriginalSubs = -> [Pocket036,Fillet028]
  Originals = -> [Pocket036,Fillet028]
  ParallelTransform = true
  Refine = true
  SubTransform = true
  Suppress = false
  TreeRank = 151
  ValidateShape = true
  _Version = 3
FEATURE [PartDesign::Body] Body039  label="Plate"
  AutoGroupSolids = false
  ClaimAllChildren = false
  ExportMode = 0
  Group = -> [Binder005,Sketch078,Pad046,Sketch081,Pocket036,Fillet028,PolarPattern017]
  InvalidShape = false
  Origin = -> Origin061
  SingleSolid = true
  Tip = -> PolarPattern017
  TreeRank = 132
  ValidateShape = true
  _ExportChildren = -> [Binder005,Pad046,Pocket036,Fillet028,PolarPattern017]
  _GroupVersion = 1
PROVENANCE & LICENSES
A FreeCAD (.FCStd) document from a public repository crawl; recipes are the document's own serialized feature recipes (and, for linked parts, companion documents' recipes).
License: as declared in the source repository (recorded in the dataset sidecar).
